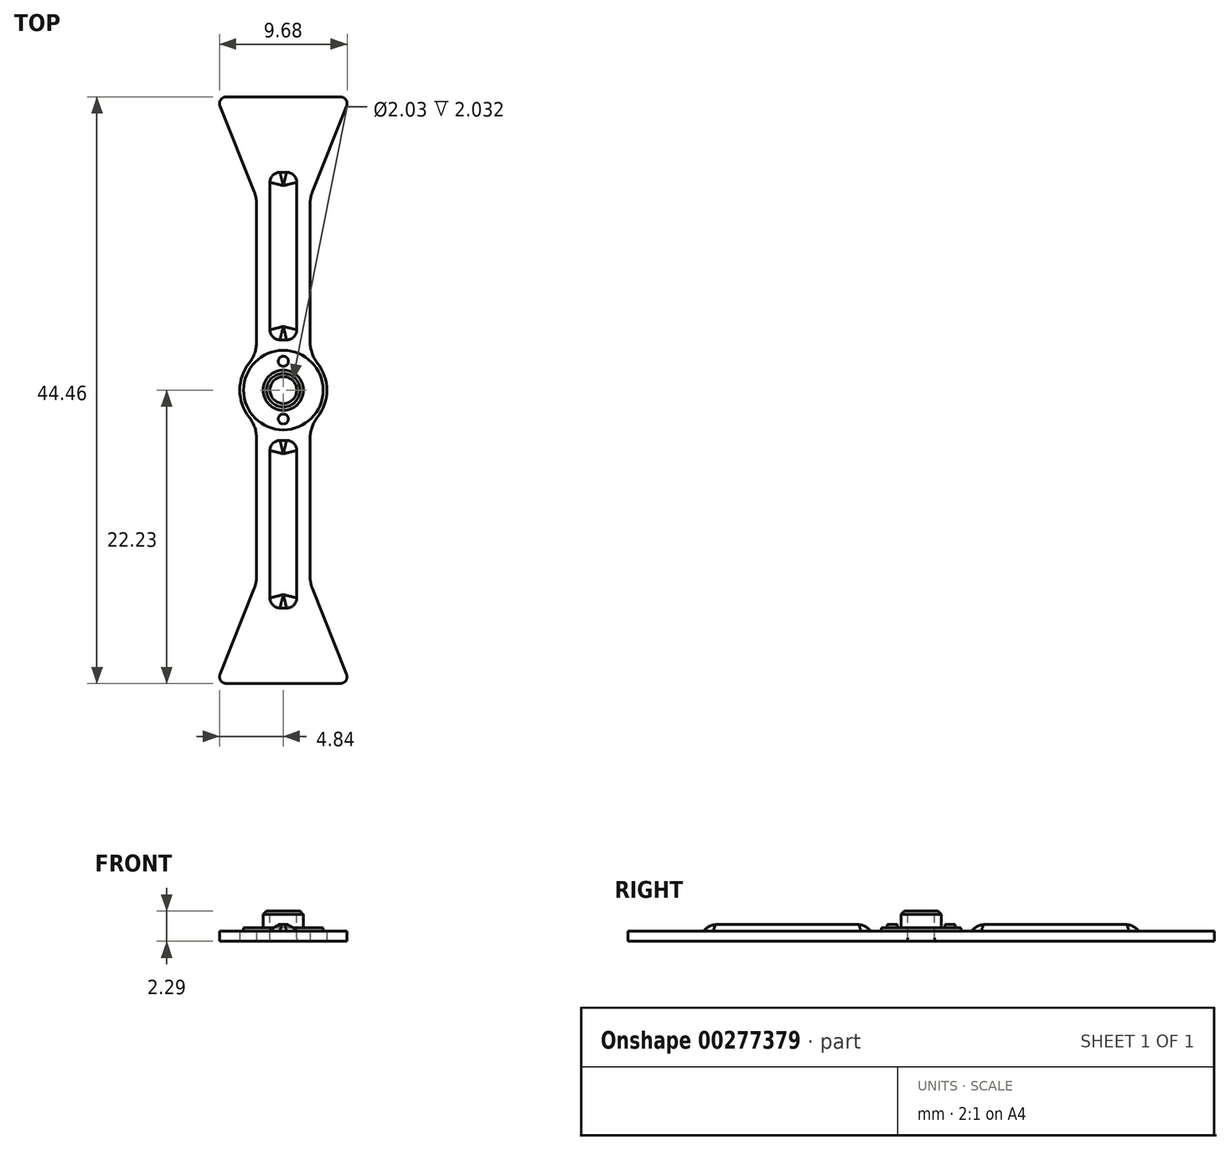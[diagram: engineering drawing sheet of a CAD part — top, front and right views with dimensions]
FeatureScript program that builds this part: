
annotation { "Feature Type Name" : "Feature", "Feature Type Description" : "" }
export const myFeature = defineFeature(function(context is Context, id is Id, definition is map)
    precondition{}
    {
        {
            var Q0;
            Q0=qCreatedBy(makeId("Top.planeOp"),FACE);
            var sketch = newSketch(context, id + "F0", { "sketchPlane" : qUnion([Q0])});
            skArc(sketch, "E0", {"start": v(2.03, -2.6) * mm, "mid": v(3.3, 0) * mm, "end": v(2.03, 2.6) * mm});
            skLineSegment(sketch, "E1", {"start": v(-2.03, 14.6) * mm, "end": v(-2.03, 2.6) * mm});
            skLineSegment(sketch, "E2", {"start": v(2.03, 14.6) * mm, "end": v(2.03, 2.6) * mm});
            skLineSegment(sketch, "E3", {"start": v(-5.08, 22.22) * mm, "end": v(5.08, 22.22) * mm});
            skLineSegment(sketch, "E4", {"start": v(-5.08, -22.23) * mm, "end": v(5.08, -22.22) * mm});
            skLineSegment(sketch, "E5", {"start": v(-5.08, 22.23) * mm, "end": v(-2.03, 14.6) * mm});
            skLineSegment(sketch, "E6", {"start": v(5.08, 22.22) * mm, "end": v(2.03, 14.6) * mm});
            skLineSegment(sketch, "E7", {"start": v(-5.08, -22.23) * mm, "end": v(-2.03, -14.6) * mm});
            skLineSegment(sketch, "E8", {"start": v(2.03, -14.6) * mm, "end": v(5.08, -22.23) * mm});
            skPoint(sketch, "E9.orphan", {"position": v(-2.03, -22.23) * mm});
            skPoint(sketch, "E10.orphan", {"position": v(2.03, -22.22) * mm});
            skArc(sketch, "E11.trimOffspring", {"start": v(-2.03, 2.6) * mm, "mid": v(-3.3, 0) * mm, "end": v(-2.03, -2.6) * mm});
            skLineSegment(sketch, "E12.trimOffspring", {"start": v(-2.03, -2.6) * mm, "end": v(-2.03, -14.6) * mm});
            skLineSegment(sketch, "E13.trimOffspring", {"start": v(2.03, -2.6) * mm, "end": v(2.03, -14.6) * mm});
            skPoint(sketch, "E14.orphan", {"position": v(-2.03, 22.22) * mm});
            skPoint(sketch, "E15.orphan", {"position": v(2.03, 22.23) * mm});
            skSolve(sketch);
        }
        {
            var Q0;
            Q0 = qSketchRegion(id + "F0", true);
            extrude(context, id + "F1", {"entities" : qUnion([Q0]), "depth" : 0.76 * mm});
        }
        {
            var Q0;
            Q0=makeQuery(id+"F1.opExtrude","SWEPT_EDGE",EDGE,{"disambiguationData":[OSD([sQuery(id+"F0.wireOp",EDGE,"E1"),sQuery(id+"F0.wireOp",EDGE,"E11.trimOffspring")])]});
            var Q1;
            Q1=makeQuery(id+"F1.opExtrude","SWEPT_EDGE",EDGE,{"disambiguationData":[OSD([sQuery(id+"F0.wireOp",EDGE,"E11.trimOffspring"),sQuery(id+"F0.wireOp",EDGE,"E12.trimOffspring")])]});
            var Q2;
            Q2=makeQuery(id+"F1.opExtrude","SWEPT_EDGE",EDGE,{"disambiguationData":[OSD([sQuery(id+"F0.wireOp",EDGE,"E0"),sQuery(id+"F0.wireOp",EDGE,"E2")])]});
            var Q3;
            Q3=makeQuery(id+"F1.opExtrude","SWEPT_EDGE",EDGE,{"disambiguationData":[OSD([sQuery(id+"F0.wireOp",EDGE,"E0"),sQuery(id+"F0.wireOp",EDGE,"E13.trimOffspring")])]});
            var Q4;
            Q4=makeQuery(id+"F1.opExtrude","SWEPT_EDGE",EDGE,{"disambiguationData":[OSD([sQuery(id+"F0.wireOp",EDGE,"E8"),sQuery(id+"F0.wireOp",EDGE,"E13.trimOffspring")])]});
            var Q5;
            Q5=makeQuery(id+"F1.opExtrude","SWEPT_EDGE",EDGE,{"disambiguationData":[OSD([sQuery(id+"F0.wireOp",EDGE,"E7"),sQuery(id+"F0.wireOp",EDGE,"E12.trimOffspring")])]});
            var Q6;
            Q6=makeQuery(id+"F1.opExtrude","SWEPT_EDGE",EDGE,{"disambiguationData":[OSD([sQuery(id+"F0.wireOp",EDGE,"E1"),sQuery(id+"F0.wireOp",EDGE,"E5")])]});
            var Q7;
            Q7=makeQuery(id+"F1.opExtrude","SWEPT_EDGE",EDGE,{"disambiguationData":[OSD([sQuery(id+"F0.wireOp",EDGE,"E2"),sQuery(id+"F0.wireOp",EDGE,"E6")])]});
            fillet(context, id + "F2", {"entities" : qUnion([Q0, Q1, Q2, Q3, Q4, Q5, Q6, Q7]), "radius" : 2.54 * mm, "tangentPropagation" : true, "allowEdgeOverflow" : false});
        }
        {
            var Q0;
            Q0=makeQuery(id+"F1.opExtrude","SWEPT_EDGE",EDGE,{"disambiguationData":[OSD([sQuery(id+"F0.wireOp",EDGE,"E3"),sQuery(id+"F0.wireOp",EDGE,"E5")])]});
            var Q1;
            Q1=makeQuery(id+"F1.opExtrude","SWEPT_EDGE",EDGE,{"disambiguationData":[OSD([sQuery(id+"F0.wireOp",EDGE,"E3"),sQuery(id+"F0.wireOp",EDGE,"E6")])]});
            var Q2;
            Q2=makeQuery(id+"F1.opExtrude","SWEPT_EDGE",EDGE,{"disambiguationData":[OSD([sQuery(id+"F0.wireOp",EDGE,"E4"),sQuery(id+"F0.wireOp",EDGE,"E8")])]});
            var Q3;
            Q3=makeQuery(id+"F1.opExtrude","SWEPT_EDGE",EDGE,{"disambiguationData":[OSD([sQuery(id+"F0.wireOp",EDGE,"E4"),sQuery(id+"F0.wireOp",EDGE,"E7")])]});
            fillet(context, id + "F3", {"entities" : qUnion([Q0, Q1, Q2, Q3]), "radius" : 0.5 * mm, "tangentPropagation" : true, "allowEdgeOverflow" : false});
        }
        {
            var Q0;
            Q0=makeQuery(id+"F1.opExtrude","CAP_FACE",FACE,{"disambiguationData":[OSD([sQuery(id+"F0.wireOp",EDGE,"E0"),sQuery(id+"F0.wireOp",EDGE,"E1"),sQuery(id+"F0.wireOp",EDGE,"E2"),sQuery(id+"F0.wireOp",EDGE,"E3"),sQuery(id+"F0.wireOp",EDGE,"E4"),sQuery(id+"F0.wireOp",EDGE,"E5"),sQuery(id+"F0.wireOp",EDGE,"E6"),sQuery(id+"F0.wireOp",EDGE,"E7"),sQuery(id+"F0.wireOp",EDGE,"E8"),sQuery(id+"F0.wireOp",EDGE,"E11.trimOffspring"),sQuery(id+"F0.wireOp",EDGE,"E12.trimOffspring"),sQuery(id+"F0.wireOp",EDGE,"E13.trimOffspring")])],"isStart":false});
            var sketch = newSketch(context, id + "F4", { "sketchPlane" : qUnion([Q0])});
            skCircle(sketch, "E16", {"center": v(0, 0) * mm, "radius": 3.01 * mm});
            skSolve(sketch);
        }
        {
            var Q0;
            Q0 = qSketchRegion(id + "F4", true);
            extrude(context, id + "F5", {"entities" : qUnion([Q0]), "operationType" : NewBodyOperationType.ADD, "depth" : 0.25 * mm});
        }
        {
            var Q0;
            Q0=makeQuery(id+"F5.opExtrude","CAP_FACE",FACE,{"disambiguationData":[OSD([sQuery(id+"F4.wireOp",EDGE,"E16")])],"isStart":false});
            var sketch = newSketch(context, id + "F6", { "sketchPlane" : qUnion([Q0])});
            skCircle(sketch, "E17", {"center": v(0, 0) * mm, "radius": 1.52 * mm});
            skSolve(sketch);
        }
        {
            var Q0;
            Q0 = qSketchRegion(id + "F6", true);
            extrude(context, id + "F7", {"entities" : qUnion([Q0]), "operationType" : NewBodyOperationType.ADD, "depth" : 1.27 * mm});
        }
        {
            var Q0;
            Q0=makeQuery(id+"F7.opExtrude","CAP_EDGE",EDGE,{"disambiguationData":[OSD([sQuery(id+"F6.wireOp",EDGE,"E17")])],"isStart":false});
            chamfer(context, id + "F8", {"entities" : qUnion([Q0]), "width" : 0.25 * mm, "tangentPropagation" : true});
        }
        {
            var Q0;
            Q0=makeQuery(id+"F5.opExtrude","CAP_FACE",FACE,{"disambiguationData":[OSD([sQuery(id+"F4.wireOp",EDGE,"E16")])],"isStart":false});
            var sketch = newSketch(context, id + "F9", { "sketchPlane" : qUnion([Q0])});
            skCircle(sketch, "E18", {"center": v(0, 2.18) * mm, "radius": 0.38 * mm});
            skCircle(sketch, "E19", {"center": v(0, -2.18) * mm, "radius": 0.38 * mm});
            skSolve(sketch);
        }
        {
            var Q0;
            Q0 = qSketchRegion(id + "F9", true);
            extrude(context, id + "F10", {"entities" : qUnion([Q0]), "operationType" : NewBodyOperationType.ADD, "depth" : 0.25 * mm});
        }
        {
            var Q0;
            Q0=makeQuery(id+"F7.opExtrude","CAP_FACE",FACE,{"disambiguationData":[OSD([sQuery(id+"F6.wireOp",EDGE,"E17")])],"isStart":false});
            var sketch = newSketch(context, id + "F11", { "sketchPlane" : qUnion([Q0]), "disableImprinting" : false});
            skCircle(sketch, "E20", {"center": v(0, 0) * mm, "radius": 1.02 * mm});
            skSolve(sketch);
        }
        {
            var Q0;
            Q0 = qSketchRegion(id + "F11", true);
            extrude(context, id + "F12", {"entities" : qUnion([Q0]), "operationType" : NewBodyOperationType.REMOVE, "oppositeDirection" : true, "depth" : 25.4 * mm});
        }
        {
            var Q0;
            Q0=makeQuery(id+"F12.boolean.opBoolean","COPY",EDGE,{"derivedFrom":makeQuery(id+"F12.opExtrude","CAP_EDGE",EDGE,{"disambiguationData":[OSD([sQuery(id+"F11.wireOp",EDGE,"E20")])],"isStart":true})});
            var Q1;
            Q1=makeQuery(id+"F12.boolean.opBoolean","INTERSECT",EDGE,{"derivedFrom":[makeQuery(id+"F1.opExtrude","CAP_FACE",FACE,{"disambiguationData":[OSD([sQuery(id+"F0.wireOp",EDGE,"E0"),sQuery(id+"F0.wireOp",EDGE,"E1"),sQuery(id+"F0.wireOp",EDGE,"E2"),sQuery(id+"F0.wireOp",EDGE,"E3"),sQuery(id+"F0.wireOp",EDGE,"E4"),sQuery(id+"F0.wireOp",EDGE,"E5"),sQuery(id+"F0.wireOp",EDGE,"E6"),sQuery(id+"F0.wireOp",EDGE,"E7"),sQuery(id+"F0.wireOp",EDGE,"E8"),sQuery(id+"F0.wireOp",EDGE,"E11.trimOffspring"),sQuery(id+"F0.wireOp",EDGE,"E12.trimOffspring"),sQuery(id+"F0.wireOp",EDGE,"E13.trimOffspring")])],"isStart":true}),makeQuery(id+"F12.opExtrude","SWEPT_FACE",FACE,{"disambiguationData":[OSD([sQuery(id+"F11.wireOp",EDGE,"E20")])]})]});
            fillet(context, id + "F13", {"entities" : qUnion([Q0, Q1]), "radius" : 0.25 * mm, "tangentPropagation" : true, "allowEdgeOverflow" : false});
        }
        {
            var Q0;
            Q0=makeQuery(id+"F1.opExtrude","CAP_FACE",FACE,{"disambiguationData":[OSD([sQuery(id+"F0.wireOp",EDGE,"E0"),sQuery(id+"F0.wireOp",EDGE,"E1"),sQuery(id+"F0.wireOp",EDGE,"E2"),sQuery(id+"F0.wireOp",EDGE,"E3"),sQuery(id+"F0.wireOp",EDGE,"E4"),sQuery(id+"F0.wireOp",EDGE,"E5"),sQuery(id+"F0.wireOp",EDGE,"E6"),sQuery(id+"F0.wireOp",EDGE,"E7"),sQuery(id+"F0.wireOp",EDGE,"E8"),sQuery(id+"F0.wireOp",EDGE,"E11.trimOffspring"),sQuery(id+"F0.wireOp",EDGE,"E12.trimOffspring"),sQuery(id+"F0.wireOp",EDGE,"E13.trimOffspring")])],"isStart":false});
            var sketch = newSketch(context, id + "F14", { "sketchPlane" : qUnion([Q0])});
            skLineSegment(sketch, "E21.bottom", {"start": v(-0.25, 16.51) * mm, "end": v(0.25, 16.51) * mm});
            skLineSegment(sketch, "E21.top", {"start": v(-0.25, 3.81) * mm, "end": v(0.25, 3.81) * mm});
            skLineSegment(sketch, "E21.left", {"start": v(-1.02, 15.75) * mm, "end": v(-1.02, 4.57) * mm});
            skLineSegment(sketch, "E21.right", {"start": v(1.02, 15.75) * mm, "end": v(1.02, 4.57) * mm});
            skLineSegment(sketch, "E22.bottom", {"start": v(-0.25, -3.81) * mm, "end": v(0.25, -3.81) * mm});
            skLineSegment(sketch, "E22.top", {"start": v(-0.25, -16.51) * mm, "end": v(0.25, -16.51) * mm});
            skLineSegment(sketch, "E22.left", {"start": v(-1.02, -4.57) * mm, "end": v(-1.02, -15.75) * mm});
            skLineSegment(sketch, "E22.right", {"start": v(1.02, -4.57) * mm, "end": v(1.02, -15.75) * mm});
            skPoint(sketch, "E23.visualSharp", {"position": v(-1.02, -3.81) * mm});
            skArc(sketch, "E23.filletArc", {"start": v(-0.25, -3.81) * mm, "mid": v(-0.8, -4.03) * mm, "end": v(-1.02, -4.57) * mm});
            skPoint(sketch, "E24.visualSharp", {"position": v(1.02, -3.81) * mm});
            skArc(sketch, "E24.filletArc", {"start": v(1.02, -4.57) * mm, "mid": v(0.8, -4.03) * mm, "end": v(0.25, -3.81) * mm});
            skPoint(sketch, "E25.visualSharp", {"position": v(-1.02, -16.51) * mm});
            skArc(sketch, "E25.filletArc", {"start": v(-1.02, -15.75) * mm, "mid": v(-0.8, -16.29) * mm, "end": v(-0.25, -16.51) * mm});
            skPoint(sketch, "E26.visualSharp", {"position": v(1.02, -16.51) * mm});
            skArc(sketch, "E26.filletArc", {"start": v(0.25, -16.51) * mm, "mid": v(0.8, -16.29) * mm, "end": v(1.02, -15.75) * mm});
            skPoint(sketch, "E27.visualSharp", {"position": v(1.02, 3.81) * mm});
            skArc(sketch, "E27.filletArc", {"start": v(0.25, 3.81) * mm, "mid": v(0.8, 4.03) * mm, "end": v(1.02, 4.57) * mm});
            skPoint(sketch, "E28.visualSharp", {"position": v(-1.02, 3.81) * mm});
            skArc(sketch, "E28.filletArc", {"start": v(-1.02, 4.57) * mm, "mid": v(-0.8, 4.03) * mm, "end": v(-0.25, 3.81) * mm});
            skPoint(sketch, "E29.visualSharp", {"position": v(-1.02, 16.51) * mm});
            skArc(sketch, "E29.filletArc", {"start": v(-0.25, 16.51) * mm, "mid": v(-0.8, 16.29) * mm, "end": v(-1.02, 15.75) * mm});
            skPoint(sketch, "E30.visualSharp", {"position": v(1.02, 16.51) * mm});
            skArc(sketch, "E30.filletArc", {"start": v(1.02, 15.75) * mm, "mid": v(0.8, 16.29) * mm, "end": v(0.25, 16.51) * mm});
            skSolve(sketch);
        }
        {
            var Q0;
            Q0 = qSketchRegion(id + "F14", true);
            extrude(context, id + "F15", {"entities" : qUnion([Q0]), "operationType" : NewBodyOperationType.ADD, "depth" : 0.5 * mm});
        }
        {
            var Q0;
            Q0=makeQuery(id+"F15.opExtrude","CAP_FACE",FACE,{"disambiguationData":[OSD([sQuery(id+"F14.wireOp",EDGE,"E21.left"),sQuery(id+"F14.wireOp",EDGE,"E21.right"),sQuery(id+"F14.wireOp",EDGE,"E27.filletArc"),sQuery(id+"F14.wireOp",EDGE,"E28.filletArc"),sQuery(id+"F14.wireOp",EDGE,"E29.filletArc"),sQuery(id+"F14.wireOp",EDGE,"E30.filletArc")])],"isStart":false});
            var Q1;
            Q1=makeQuery(id+"F15.opExtrude","CAP_FACE",FACE,{"disambiguationData":[OSD([sQuery(id+"F14.wireOp",EDGE,"E22.left"),sQuery(id+"F14.wireOp",EDGE,"E22.right"),sQuery(id+"F14.wireOp",EDGE,"E23.filletArc"),sQuery(id+"F14.wireOp",EDGE,"E24.filletArc"),sQuery(id+"F14.wireOp",EDGE,"E25.filletArc"),sQuery(id+"F14.wireOp",EDGE,"E26.filletArc")])],"isStart":false});
            fillet(context, id + "F16", {"entities" : qUnion([Q0, Q1]), "radius" : 1.27 * mm, "tangentPropagation" : true, "allowEdgeOverflow" : false});
        }
    });
